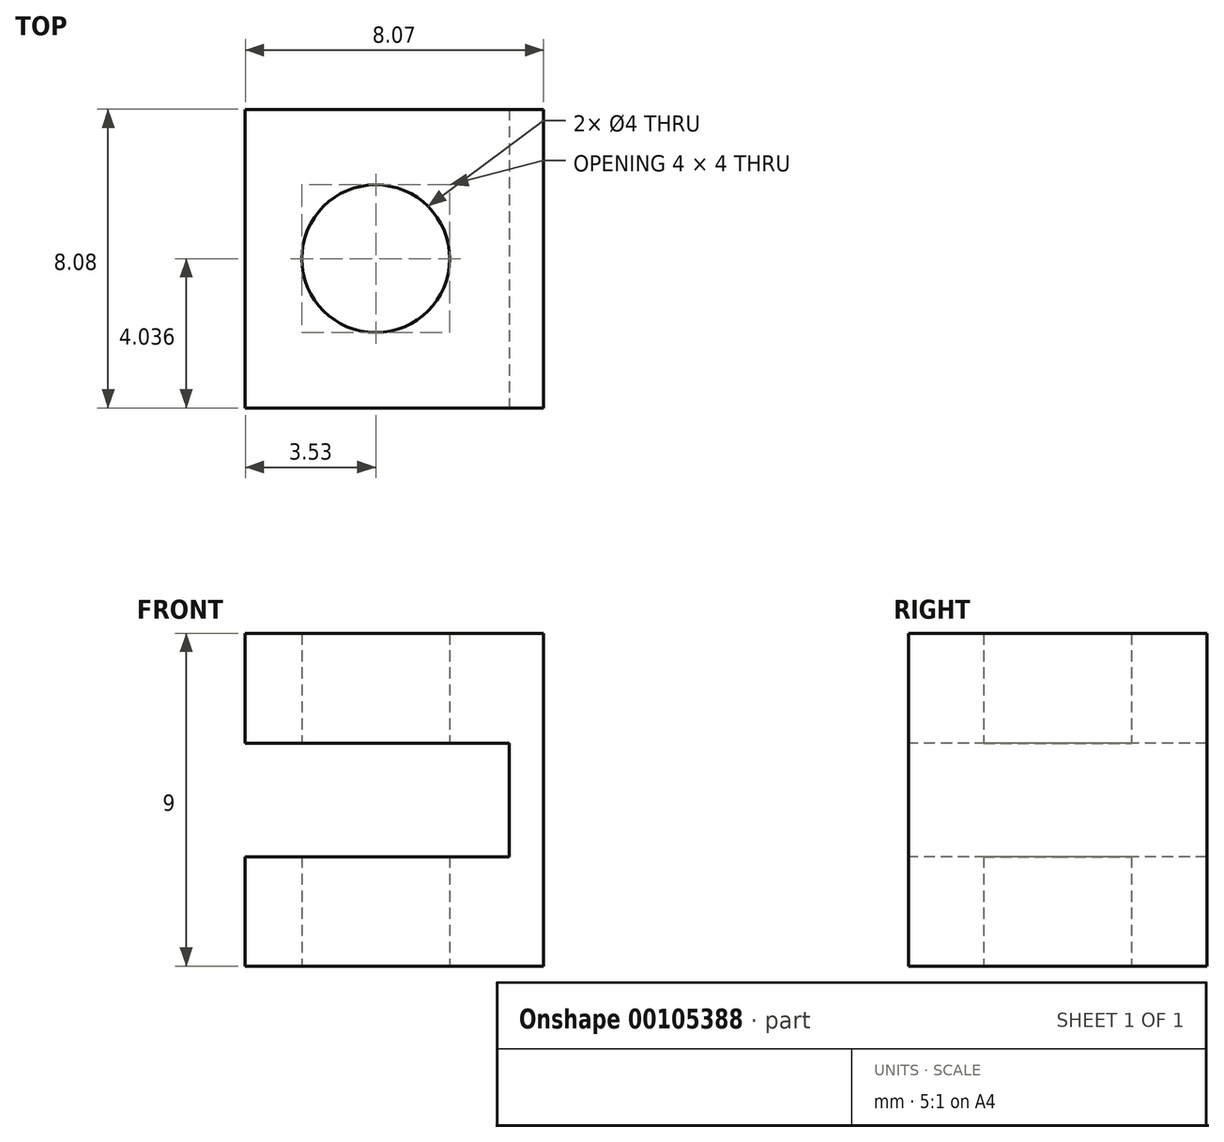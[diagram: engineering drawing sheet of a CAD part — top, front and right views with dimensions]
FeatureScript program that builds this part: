
annotation { "Feature Type Name" : "Feature", "Feature Type Description" : "" }
export const myFeature = defineFeature(function(context is Context, id is Id, definition is map)
    precondition{}
    {
        {
            var Q0;
            Q0=qCreatedBy(makeId("Top.planeOp"),FACE);
            var sketch = newSketch(context, id + "F0", { "sketchPlane" : qUnion([Q0])});
            skCircle(sketch, "E0", {"center": v(-36.12, 15.47) * mm, "radius": 3.5 * mm});
            skCircle(sketch, "E1.cCircle", {"center": v(-36.12, 15.47) * mm, "radius": 3.5 * mm, "construction": true});
            skLineSegment(sketch, "E1.0", {"start": v(-39.58, 13.38) * mm, "end": v(-39.65, 17.43) * mm});
            skLineSegment(sketch, "E1.1", {"start": v(-39.65, 17.43) * mm, "end": v(-36.2, 19.5) * mm});
            skLineSegment(sketch, "E1.2", {"start": v(-36.2, 19.5) * mm, "end": v(-32.66, 17.55) * mm});
            skLineSegment(sketch, "E1.3", {"start": v(-32.66, 17.55) * mm, "end": v(-32.58, 13.5) * mm});
            skLineSegment(sketch, "E1.4", {"start": v(-32.58, 13.5) * mm, "end": v(-36.05, 11.43) * mm});
            skLineSegment(sketch, "E1.5", {"start": v(-36.05, 11.43) * mm, "end": v(-39.58, 13.38) * mm});
            skPoint(sketch, "E1.0.midPoint", {"position": v(-39.62, 15.4) * mm});
            skCircle(sketch, "E2", {"center": v(-36.12, 15.47) * mm, "radius": 2 * mm});
            skLineSegment(sketch, "E3.bottom", {"start": v(-32.58, 11.43) * mm, "end": v(-39.65, 11.43) * mm});
            skLineSegment(sketch, "E3.top", {"start": v(-32.58, 19.5) * mm, "end": v(-39.65, 19.5) * mm});
            skLineSegment(sketch, "E3.left", {"start": v(-32.58, 11.43) * mm, "end": v(-32.58, 19.5) * mm});
            skLineSegment(sketch, "E3.right", {"start": v(-39.65, 11.43) * mm, "end": v(-39.65, 19.5) * mm});
            skLineSegment(sketch, "E4.bottom", {"start": v(-32.58, 19.5) * mm, "end": v(-31.58, 19.5) * mm});
            skLineSegment(sketch, "E4.top", {"start": v(-32.58, 11.43) * mm, "end": v(-31.58, 11.43) * mm});
            skLineSegment(sketch, "E4.left", {"start": v(-32.58, 19.5) * mm, "end": v(-32.58, 11.43) * mm});
            skLineSegment(sketch, "E4.right", {"start": v(-31.58, 19.5) * mm, "end": v(-31.58, 11.43) * mm});
            skSolve(sketch);
        }
        {
            var Q0;
            {var subQ0=sQuery(id+"F0.wireOp",EDGE,"E1.1");var subQ1=sQuery(id+"F0.wireOp",EDGE,"E0");var subQ2=makeQuery(id+"F0.imprint","INTERSECT",VERTEX,{"derivedFrom":[subQ1,subQ0]});Q0=makeQuery(id+"F0.imprint","IMPRINT",FACE,{"disambiguationData":[TD([[makeQuery(id+"F0.imprint","IMPRINT",EDGE,{"disambiguationData":[TD([[subQ2,-1.0]])],"derivedFrom":subQ1}),-1.0]])]});}
            var Q1;
            {var subQ0=sQuery(id+"F0.wireOp",EDGE,"E1.0");var subQ1=sQuery(id+"F0.wireOp",EDGE,"E0");var subQ2=makeQuery(id+"F0.imprint","INTERSECT",VERTEX,{"derivedFrom":[subQ1,subQ0]});Q1=makeQuery(id+"F0.imprint","IMPRINT",FACE,{"disambiguationData":[TD([[makeQuery(id+"F0.imprint","IMPRINT",EDGE,{"disambiguationData":[TD([[subQ2,-1.0]])],"derivedFrom":subQ1}),-1.0]])]});}
            var Q2;
            {var subQ0=sQuery(id+"F0.wireOp",EDGE,"E1.5");var subQ1=sQuery(id+"F0.wireOp",EDGE,"E0");var subQ2=makeQuery(id+"F0.imprint","INTERSECT",VERTEX,{"derivedFrom":[subQ1,subQ0]});Q2=makeQuery(id+"F0.imprint","IMPRINT",FACE,{"disambiguationData":[TD([[makeQuery(id+"F0.imprint","IMPRINT",EDGE,{"disambiguationData":[TD([[subQ2,-1.0]])],"derivedFrom":subQ1}),-1.0]])]});}
            var Q3;
            {var subQ0=sQuery(id+"F0.wireOp",EDGE,"E1.4");var subQ1=sQuery(id+"F0.wireOp",EDGE,"E0");var subQ2=makeQuery(id+"F0.imprint","INTERSECT",VERTEX,{"derivedFrom":[subQ1,subQ0]});Q3=makeQuery(id+"F0.imprint","IMPRINT",FACE,{"disambiguationData":[TD([[makeQuery(id+"F0.imprint","IMPRINT",EDGE,{"disambiguationData":[TD([[subQ2,-1.0]])],"derivedFrom":subQ1}),-1.0]])]});}
            var Q4;
            {var subQ0=sQuery(id+"F0.wireOp",EDGE,"E1.2");var subQ1=sQuery(id+"F0.wireOp",EDGE,"E0");var subQ2=makeQuery(id+"F0.imprint","INTERSECT",VERTEX,{"derivedFrom":[subQ1,subQ0]});Q4=makeQuery(id+"F0.imprint","IMPRINT",FACE,{"disambiguationData":[TD([[makeQuery(id+"F0.imprint","IMPRINT",EDGE,{"disambiguationData":[TD([[subQ2,1.0]])],"derivedFrom":subQ1}),-1.0]])]});}
            var Q5;
            {var subQ0=sQuery(id+"F0.wireOp",EDGE,"E1.1");var subQ1=sQuery(id+"F0.wireOp",EDGE,"E0");var subQ2=makeQuery(id+"F0.imprint","INTERSECT",VERTEX,{"derivedFrom":[subQ1,subQ0]});Q5=makeQuery(id+"F0.imprint","IMPRINT",FACE,{"disambiguationData":[TD([[makeQuery(id+"F0.imprint","IMPRINT",EDGE,{"disambiguationData":[TD([[subQ2,1.0]])],"derivedFrom":subQ1}),-1.0]])]});}
            var Q6;
            Q6=makeQuery(id+"F0.imprint","IMPRINT",FACE,{"disambiguationData":[TD([[makeQuery(id+"F0.imprint","IMPRINT",EDGE,{"derivedFrom":sQuery(id+"F0.wireOp",EDGE,"E2")}),-1.0]])]});
            extrude(context, id + "F1", {"entities" : qUnion([Q0, Q1, Q2, Q3, Q4, Q5, Q6]), "depth" : 6 * mm, "hasSecondDirection" : true, "secondDirectionOppositeDirection" : false, "secondDirectionDepth" : 3 * mm});
        }
        {
            var Q0;
            {var subQ0=sQuery(id+"F0.wireOp",EDGE,"E1.1");var subQ1=sQuery(id+"F0.wireOp",EDGE,"E0");var subQ2=makeQuery(id+"F0.imprint","INTERSECT",VERTEX,{"derivedFrom":[subQ1,subQ0]});Q0=makeQuery(id+"F0.imprint","IMPRINT",FACE,{"disambiguationData":[TD([[makeQuery(id+"F0.imprint","IMPRINT",EDGE,{"disambiguationData":[TD([[subQ2,-1.0]])],"derivedFrom":subQ1}),-1.0]])]});}
            var Q1;
            {var subQ1=sQuery(id+"F0.wireOp",EDGE,"E1.5");var subQ6=sQuery(id+"F0.wireOp",EDGE,"E1.0");var subQ9=makeQuery(id+"F0.imprint","INTERSECT",VERTEX,{"derivedFrom":[subQ6,subQ1]});Q1=makeQuery(id+"F0.imprint","IMPRINT",FACE,{"disambiguationData":[TD([[makeQuery(id+"F0.imprint","IMPRINT",EDGE,{"disambiguationData":[TD([[subQ9,-1.0]])],"derivedFrom":subQ6}),1.0]])]});}
            var Q2;
            {var subQ1=sQuery(id+"F0.wireOp",EDGE,"E1.4");var subQ3=makeQuery(id+"F0.imprint","INTERSECT",VERTEX,{"derivedFrom":[sQuery(id+"F0.wireOp",EDGE,"E0"),subQ1]});Q2=makeQuery(id+"F0.imprint","IMPRINT",FACE,{"disambiguationData":[TD([[makeQuery(id+"F0.imprint","IMPRINT",EDGE,{"disambiguationData":[TD([[subQ3,1.0]])],"derivedFrom":subQ1}),1.0]])]});}
            var Q3;
            Q3=makeQuery(id+"F0.imprint","IMPRINT",FACE,{"disambiguationData":[TD([[makeQuery(id+"F0.imprint","IMPRINT",EDGE,{"derivedFrom":sQuery(id+"F0.wireOp",EDGE,"E2")}),-1.0]])]});
            var Q4;
            {var subQ0=sQuery(id+"F0.wireOp",EDGE,"E1.4");var subQ1=sQuery(id+"F0.wireOp",EDGE,"E0");var subQ2=makeQuery(id+"F0.imprint","INTERSECT",VERTEX,{"derivedFrom":[subQ1,subQ0]});Q4=makeQuery(id+"F0.imprint","IMPRINT",FACE,{"disambiguationData":[TD([[makeQuery(id+"F0.imprint","IMPRINT",EDGE,{"disambiguationData":[TD([[subQ2,-1.0]])],"derivedFrom":subQ1}),-1.0]])]});}
            var Q5;
            {var subQ1=sQuery(id+"F0.wireOp",EDGE,"E1.1");var subQ3=makeQuery(id+"F0.imprint","INTERSECT",VERTEX,{"derivedFrom":[sQuery(id+"F0.wireOp",EDGE,"E0"),subQ1]});Q5=makeQuery(id+"F0.imprint","IMPRINT",FACE,{"disambiguationData":[TD([[makeQuery(id+"F0.imprint","IMPRINT",EDGE,{"disambiguationData":[TD([[subQ3,1.0]])],"derivedFrom":subQ1}),1.0]])]});}
            var Q6;
            {var subQ3=sQuery(id+"F0.wireOp",EDGE,"E4.bottom");Q6=makeQuery(id+"F0.imprint","IMPRINT",FACE,{"disambiguationData":[TD([[makeQuery(id+"F0.imprint","IMPRINT",EDGE,{"derivedFrom":subQ3}),-1.0]])]});}
            var Q7;
            {var subQ0=sQuery(id+"F0.wireOp",EDGE,"E1.1");var subQ1=sQuery(id+"F0.wireOp",EDGE,"E0");var subQ2=makeQuery(id+"F0.imprint","INTERSECT",VERTEX,{"derivedFrom":[subQ1,subQ0]});Q7=makeQuery(id+"F0.imprint","IMPRINT",FACE,{"disambiguationData":[TD([[makeQuery(id+"F0.imprint","IMPRINT",EDGE,{"disambiguationData":[TD([[subQ2,1.0]])],"derivedFrom":subQ1}),-1.0]])]});}
            var Q8;
            {var subQ1=sQuery(id+"F0.wireOp",EDGE,"E1.3");var subQ5=sQuery(id+"F0.wireOp",EDGE,"E1.2");var subQ6=makeQuery(id+"F0.imprint","INTERSECT",VERTEX,{"derivedFrom":[subQ5,subQ1]});Q8=makeQuery(id+"F0.imprint","IMPRINT",FACE,{"disambiguationData":[TD([[makeQuery(id+"F0.imprint","IMPRINT",EDGE,{"disambiguationData":[TD([[subQ6,1.0]])],"derivedFrom":subQ5}),1.0]])]});}
            var Q9;
            {var subQ0=sQuery(id+"F0.wireOp",EDGE,"E1.5");var subQ1=sQuery(id+"F0.wireOp",EDGE,"E0");var subQ2=makeQuery(id+"F0.imprint","INTERSECT",VERTEX,{"derivedFrom":[subQ1,subQ0]});Q9=makeQuery(id+"F0.imprint","IMPRINT",FACE,{"disambiguationData":[TD([[makeQuery(id+"F0.imprint","IMPRINT",EDGE,{"disambiguationData":[TD([[subQ2,-1.0]])],"derivedFrom":subQ1}),-1.0]])]});}
            var Q10;
            {var subQ0=sQuery(id+"F0.wireOp",EDGE,"E1.0");var subQ1=sQuery(id+"F0.wireOp",EDGE,"E0");var subQ2=makeQuery(id+"F0.imprint","INTERSECT",VERTEX,{"derivedFrom":[subQ1,subQ0]});Q10=makeQuery(id+"F0.imprint","IMPRINT",FACE,{"disambiguationData":[TD([[makeQuery(id+"F0.imprint","IMPRINT",EDGE,{"disambiguationData":[TD([[subQ2,-1.0]])],"derivedFrom":subQ1}),-1.0]])]});}
            var Q11;
            {var subQ0=sQuery(id+"F0.wireOp",EDGE,"E1.2");var subQ1=sQuery(id+"F0.wireOp",EDGE,"E0");var subQ2=makeQuery(id+"F0.imprint","INTERSECT",VERTEX,{"derivedFrom":[subQ1,subQ0]});Q11=makeQuery(id+"F0.imprint","IMPRINT",FACE,{"disambiguationData":[TD([[makeQuery(id+"F0.imprint","IMPRINT",EDGE,{"disambiguationData":[TD([[subQ2,1.0]])],"derivedFrom":subQ1}),-1.0]])]});}
            extrude(context, id + "F2", {"entities" : qUnion([Q0, Q1, Q2, Q3, Q4, Q5, Q6, Q7, Q8, Q9, Q10, Q11]), "depth" : 9 * mm});
        }
        {
            var Q0;
            Q0=makeQuery(id+"F2.opExtrude","SWEPT_FACE",FACE,{"disambiguationData":[OSD([sQuery(id+"F0.wireOp",EDGE,"E3.bottom"),sQuery(id+"F0.wireOp",EDGE,"E4.top")])]});
            var sketch = newSketch(context, id + "F3", { "sketchPlane" : qUnion([Q0])});
            skLineSegment(sketch, "E5.bottom", {"start": v(-39.65, 6.03) * mm, "end": v(-32.5, 6.03) * mm});
            skLineSegment(sketch, "E5.top", {"start": v(-39.65, 2.96) * mm, "end": v(-32.5, 2.96) * mm});
            skLineSegment(sketch, "E5.left", {"start": v(-39.65, 6.03) * mm, "end": v(-39.65, 2.96) * mm});
            skLineSegment(sketch, "E5.right", {"start": v(-32.5, 6.03) * mm, "end": v(-32.5, 2.96) * mm});
            skSolve(sketch);
        }
        {
            var Q0;
            Q0=makeQuery(id+"F3.imprint","IMPRINT",FACE,{"disambiguationData":[TD([[makeQuery(id+"F3.imprint","IMPRINT",EDGE,{"derivedFrom":sQuery(id+"F3.wireOp",EDGE,"E5.bottom")}),-1.0]])]});
            extrude(context, id + "F4", {"entities" : qUnion([Q0]), "operationType" : NewBodyOperationType.REMOVE, "oppositeDirection" : true, "depth" : 25 * mm});
        }
    });
